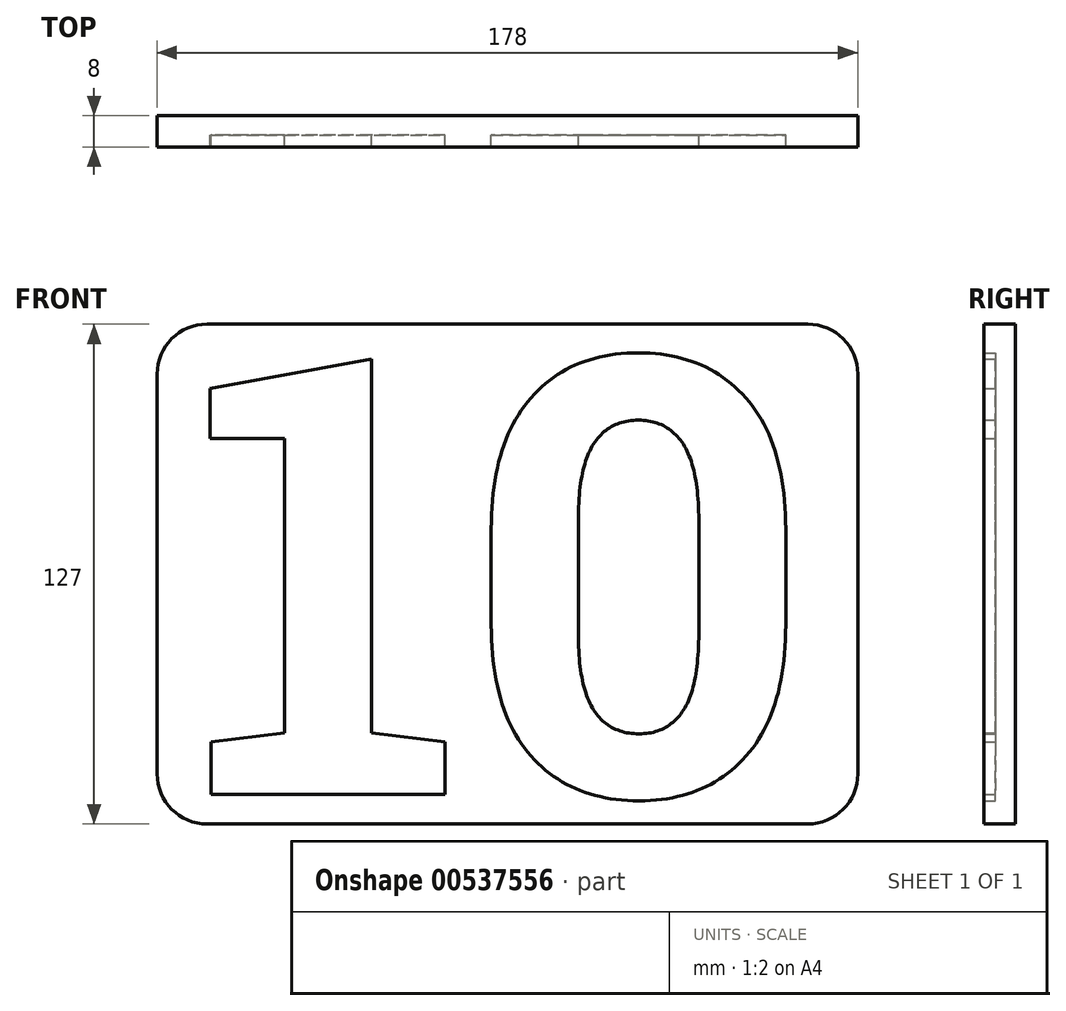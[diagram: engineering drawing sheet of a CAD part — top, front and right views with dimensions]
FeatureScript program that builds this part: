
annotation { "Feature Type Name" : "Feature", "Feature Type Description" : "" }
export const myFeature = defineFeature(function(context is Context, id is Id, definition is map)
    precondition{}
    {
        {
            var Q0;
            Q0=qCreatedBy(makeId("Front.planeOp"),FACE);
            var sketch = newSketch(context, id + "F0", { "sketchPlane" : qUnion([Q0])});
            skLineSegment(sketch, "E0.bottom", {"start": v(89, -63.5) * mm, "end": v(-89, -63.5) * mm});
            skLineSegment(sketch, "E0.top", {"start": v(89, 63.5) * mm, "end": v(-89, 63.5) * mm});
            skLineSegment(sketch, "E0.left", {"start": v(89, -63.5) * mm, "end": v(89, 63.5) * mm});
            skLineSegment(sketch, "E0.right", {"start": v(-89, -63.5) * mm, "end": v(-89, 63.5) * mm});
            skPoint(sketch, "E0.middle", {"position": v(0, 0) * mm});
            skText(sketch, "E1", { "text": "10", "fontName": "RobotoSlab-Bold.ttf"});
            skLineSegment(sketch, "E2", {"start": v(-80.22, 56) * mm, "end": v(-80.22, 63.5) * mm});
            skLineSegment(sketch, "E3", {"start": v(-80.22, -56) * mm, "end": v(-80.22, -63.5) * mm});
            const initialGuessF0  = {"E1": [-0.08022, -0.056, 1, 0, 0.112]};
            skSetInitialGuess(sketch, initialGuessF0);
            skSolve(sketch);
        }
        {
            var Q0;
            {var subQ3=sQuery(id+"F0.wireOp",EDGE,"E0.left");Q0=makeQuery(id+"F0.imprint","IMPRINT",FACE,{"disambiguationData":[TD([[makeQuery(id+"F0.imprint","IMPRINT",EDGE,{"derivedFrom":subQ3}),1.0]])]});}
            var Q1;
            Q1=makeQuery(id+"F0.imprint","IMPRINT",FACE,{"disambiguationData":[TD([[makeQuery(id+"F0.imprint","IMPRINT",EDGE,{"derivedFrom":sQuery(id+"F0.wireOp",EDGE,"E1.sketch_text.stroke-20")}),1.0]])]});
            var Q2;
            Q2=makeQuery(id+"F0.imprint","IMPRINT",FACE,{"disambiguationData":[TD([[makeQuery(id+"F0.imprint","IMPRINT",EDGE,{"derivedFrom":sQuery(id+"F0.wireOp",EDGE,"E1.sketch_text.stroke-10")}),-1.0]])]});
            var Q3;
            Q3=makeQuery(id+"F0.imprint","IMPRINT",FACE,{"disambiguationData":[TD([[makeQuery(id+"F0.imprint","IMPRINT",EDGE,{"derivedFrom":sQuery(id+"F0.wireOp",EDGE,"E1.sketch_text.stroke-0")}),-1.0]])]});
            extrude(context, id + "F1", {"entities" : qUnion([Q0, Q1, Q2, Q3]), "depth" : 5 * mm, "offsetDistance" : 25.4 * mm});
        }
        {
            var Q0;
            Q0=makeQuery(id+"F0.imprint","IMPRINT",FACE,{"disambiguationData":[TD([[makeQuery(id+"F0.imprint","IMPRINT",EDGE,{"derivedFrom":sQuery(id+"F0.wireOp",EDGE,"E1.sketch_text.stroke-20")}),1.0]])]});
            var Q1;
            {var subQ3=sQuery(id+"F0.wireOp",EDGE,"E0.left");Q1=makeQuery(id+"F0.imprint","IMPRINT",FACE,{"disambiguationData":[TD([[makeQuery(id+"F0.imprint","IMPRINT",EDGE,{"derivedFrom":subQ3}),1.0]])]});}
            extrude(context, id + "F2", {"entities" : qUnion([Q0, Q1]), "operationType" : NewBodyOperationType.ADD, "depth" : 8 * mm, "offsetDistance" : 25.4 * mm});
        }
        {
            var Q0;
            {var subQ0=sQuery(id+"F0.wireOp",EDGE,"E0.right");var subQ1=sQuery(id+"F0.wireOp",EDGE,"E0.top");Q0=makeQuery(id+"F2.boolean.opBoolean","MERGE",EDGE,{"derivedFrom":[makeQuery(id+"F1.opExtrude","SWEPT_EDGE",EDGE,{"disambiguationData":[OSD([subQ1,subQ0])]}),makeQuery(id+"F2.opExtrude","SWEPT_EDGE",EDGE,{"disambiguationData":[OSD([subQ1,subQ0])]})]});}
            var Q1;
            {var subQ0=sQuery(id+"F0.wireOp",EDGE,"E0.right");var subQ1=sQuery(id+"F0.wireOp",EDGE,"E0.bottom");Q1=makeQuery(id+"F2.boolean.opBoolean","MERGE",EDGE,{"derivedFrom":[makeQuery(id+"F1.opExtrude","SWEPT_EDGE",EDGE,{"disambiguationData":[OSD([subQ1,subQ0])]}),makeQuery(id+"F2.opExtrude","SWEPT_EDGE",EDGE,{"disambiguationData":[OSD([subQ1,subQ0])]})]});}
            var Q2;
            {var subQ0=sQuery(id+"F0.wireOp",EDGE,"E0.left");var subQ1=sQuery(id+"F0.wireOp",EDGE,"E0.bottom");Q2=makeQuery(id+"F2.boolean.opBoolean","MERGE",EDGE,{"derivedFrom":[makeQuery(id+"F1.opExtrude","SWEPT_EDGE",EDGE,{"disambiguationData":[OSD([subQ1,subQ0])]}),makeQuery(id+"F2.opExtrude","SWEPT_EDGE",EDGE,{"disambiguationData":[OSD([subQ1,subQ0])]})]});}
            var Q3;
            {var subQ0=sQuery(id+"F0.wireOp",EDGE,"E0.left");var subQ1=sQuery(id+"F0.wireOp",EDGE,"E0.top");Q3=makeQuery(id+"F2.boolean.opBoolean","MERGE",EDGE,{"derivedFrom":[makeQuery(id+"F1.opExtrude","SWEPT_EDGE",EDGE,{"disambiguationData":[OSD([subQ1,subQ0])]}),makeQuery(id+"F2.opExtrude","SWEPT_EDGE",EDGE,{"disambiguationData":[OSD([subQ1,subQ0])]})]});}
            fillet(context, id + "F3", {"entities" : qUnion([Q0, Q1, Q2, Q3]), "radius" : 12.7 * mm, "tangentPropagation" : true, "allowEdgeOverflow" : false});
        }
    });
